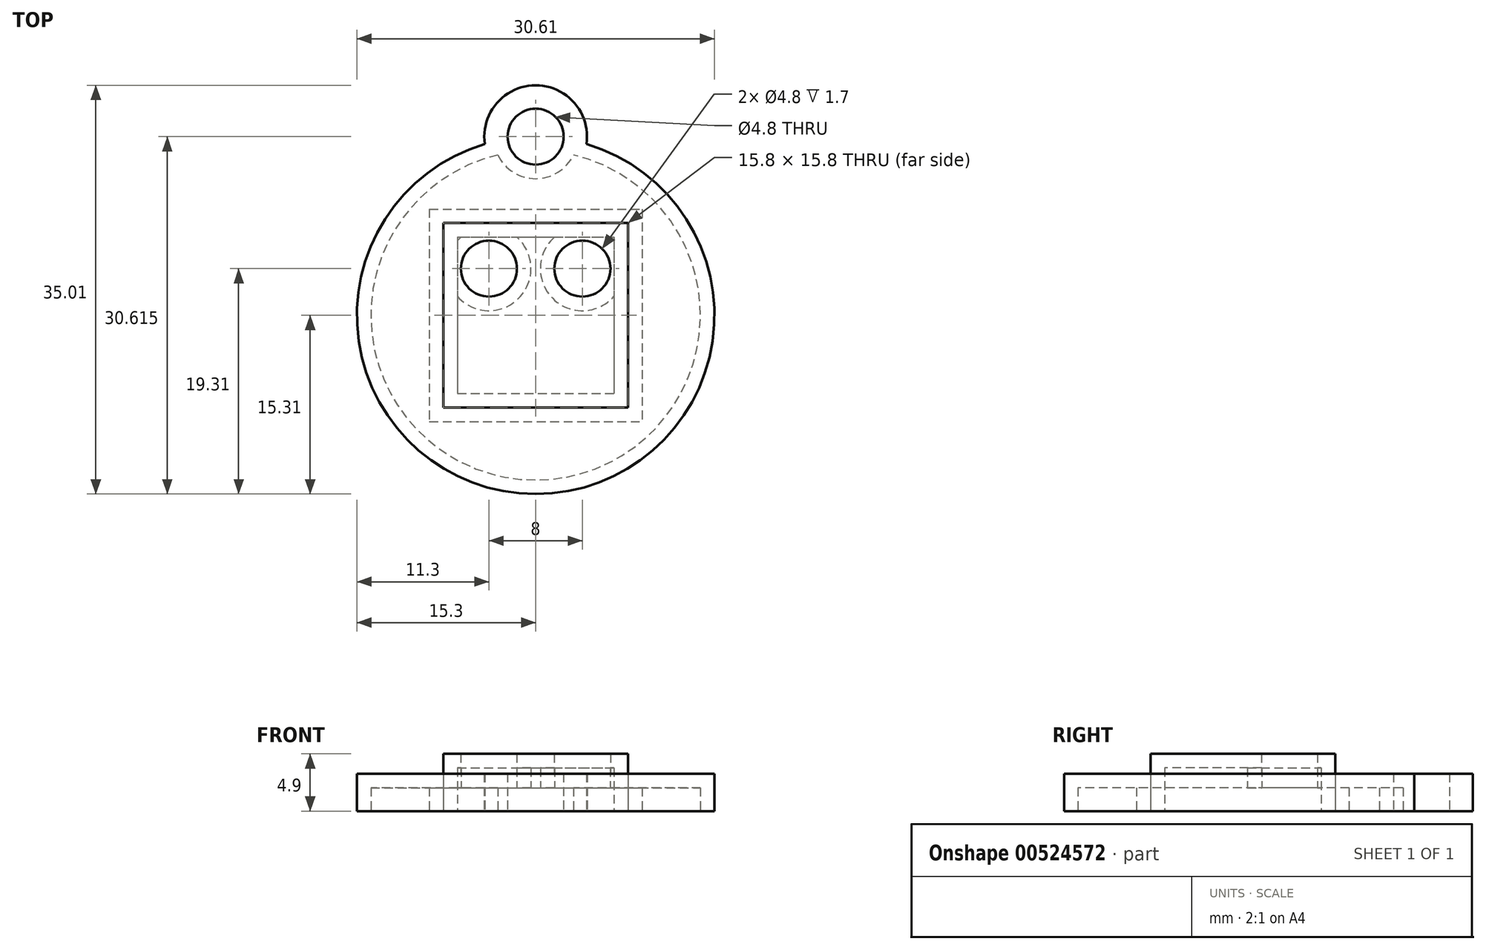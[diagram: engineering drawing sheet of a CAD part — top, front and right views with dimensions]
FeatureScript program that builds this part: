
annotation { "Feature Type Name" : "Feature", "Feature Type Description" : "" }
export const myFeature = defineFeature(function(context is Context, id is Id, definition is map)
    precondition{}
    {
        {
            var Q0;
            Q0=qCreatedBy(makeId("Top.planeOp"),FACE);
            var sketch = newSketch(context, id + "F0", { "sketchPlane" : qUnion([Q0])});
            skLineSegment(sketch, "E0.bottom", {"start": v(-7.9, 7.9) * mm, "end": v(7.9, 7.9) * mm});
            skLineSegment(sketch, "E0.top", {"start": v(-7.9, -7.9) * mm, "end": v(7.9, -7.9) * mm});
            skLineSegment(sketch, "E0.left", {"start": v(-7.9, 7.9) * mm, "end": v(-7.9, -7.9) * mm});
            skLineSegment(sketch, "E0.right", {"start": v(7.9, 7.9) * mm, "end": v(7.9, -7.9) * mm});
            skPoint(sketch, "E0.middle", {"position": v(0, 0) * mm});
            skSolve(sketch);
        }
        {
            var Q0;
            Q0=makeQuery(id+"F0.imprint","IMPRINT",FACE,{"disambiguationData":[TD([[makeQuery(id+"F0.imprint","IMPRINT",EDGE,{"derivedFrom":sQuery(id+"F0.wireOp",EDGE,"E0.bottom")}),-1.0]])]});
            extrude(context, id + "F1", {"entities" : qUnion([Q0]), "depth" : 3.2 * mm, "offsetDistance" : 25 * mm});
        }
        {
            var Q0;
            Q0=makeQuery(id+"F1.opExtrude","CAP_FACE",FACE,{"disambiguationData":[OSD([sQuery(id+"F0.wireOp",EDGE,"E0.bottom"),sQuery(id+"F0.wireOp",EDGE,"E0.top"),sQuery(id+"F0.wireOp",EDGE,"E0.left"),sQuery(id+"F0.wireOp",EDGE,"E0.right")])],"isStart":false});
            var sketch = newSketch(context, id + "F2", { "sketchPlane" : qUnion([Q0])});
            skCircle(sketch, "E1", {"center": v(-4, -4) * mm, "radius": 2.4 * mm});
            skCircle(sketch, "E2", {"center": v(4, -4) * mm, "radius": 2.4 * mm});
            skLineSegment(sketch, "E3", {"start": v(1.5, 0) * mm, "end": v(-1.5, 0) * mm, "construction": true});
            skLineSegment(sketch, "E4", {"start": v(0, -1.55) * mm, "end": v(0, 1.55) * mm, "construction": true});
            skLineSegment(sketch, "E5", {"start": v(-4, -4) * mm, "end": v(4, -4) * mm, "construction": true});
            skPoint(sketch, "E6", {"position": v(0, -4) * mm});
            skCircle(sketch, "E7.MirrorC", {"center": v(-4, 4) * mm, "radius": 2.4 * mm});
            skCircle(sketch, "E8.MirrorC", {"center": v(4, 4) * mm, "radius": 2.4 * mm});
            skLineSegment(sketch, "E9.MirrorCS", {"start": v(-4, 4) * mm, "end": v(4, 4) * mm, "construction": true});
            skPoint(sketch, "E10.MirrorP", {"position": v(0, 4) * mm});
            skPoint(sketch, "E11", {"position": v(-10.7, -6.83) * mm});
            skSolve(sketch);
        }
        {
            var Q0;
            Q0=makeQuery(id+"F2.imprint","IMPRINT",FACE,{"disambiguationData":[TD([[makeQuery(id+"F2.imprint","IMPRINT",EDGE,{"derivedFrom":sQuery(id+"F2.wireOp",EDGE,"E1")}),1.0]])]});
            var Q1;
            Q1=makeQuery(id+"F2.imprint","IMPRINT",FACE,{"disambiguationData":[TD([[makeQuery(id+"F2.imprint","IMPRINT",EDGE,{"derivedFrom":sQuery(id+"F2.wireOp",EDGE,"E7.MirrorC")}),-1.0]])]});
            var Q2;
            Q2=makeQuery(id+"F2.imprint","IMPRINT",FACE,{"disambiguationData":[TD([[makeQuery(id+"F2.imprint","IMPRINT",EDGE,{"derivedFrom":sQuery(id+"F2.wireOp",EDGE,"E8.MirrorC")}),-1.0]])]});
            var Q3;
            Q3=makeQuery(id+"F2.imprint","IMPRINT",FACE,{"disambiguationData":[TD([[makeQuery(id+"F2.imprint","IMPRINT",EDGE,{"derivedFrom":sQuery(id+"F2.wireOp",EDGE,"E2")}),1.0]])]});
            extrude(context, id + "F3", {"entities" : qUnion([Q0, Q1, Q2, Q3]), "operationType" : NewBodyOperationType.ADD, "depth" : 1.7 * mm, "offsetDistance" : 25 * mm});
        }
        {
            var Q0;
            Q0=qCreatedBy(makeId("Top.planeOp"),FACE);
            var sketch = newSketch(context, id + "F4", { "sketchPlane" : qUnion([Q0])});
            skArc(sketch, "E12", {"start": v(-4.35, 14.67) * mm, "mid": v(0, -15.3) * mm, "end": v(4.35, 14.67) * mm});
            skCircle(sketch, "E13", {"center": v(0, 15.3) * mm, "radius": 2.4 * mm});
            skArc(sketch, "E14.0", {"start": v(4.35, 14.67) * mm, "mid": v(0, 19.7) * mm, "end": v(-4.35, 14.67) * mm});
            skLineSegment(sketch, "E15.0", {"start": v(-7.9, 7.9) * mm, "end": v(7.9, 7.9) * mm});
            skLineSegment(sketch, "E16.0", {"start": v(-7.9, 7.9) * mm, "end": v(-7.9, -7.9) * mm});
            skLineSegment(sketch, "E17.0", {"start": v(-7.9, -7.9) * mm, "end": v(7.9, -7.9) * mm});
            skLineSegment(sketch, "E18.0", {"start": v(7.9, 7.9) * mm, "end": v(7.9, -7.9) * mm});
            skSolve(sketch);
        }
        {
            var Q0;
            Q0=makeQuery(id+"F4.imprint","IMPRINT",FACE,{"disambiguationData":[TD([[makeQuery(id+"F4.imprint","IMPRINT",EDGE,{"derivedFrom":sQuery(id+"F4.wireOp",EDGE,"E12")}),1.0]])]});
            extrude(context, id + "F5", {"entities" : qUnion([Q0]), "depth" : 3.2 * mm, "offsetDistance" : 25 * mm});
        }
        {
            var Q0;
            Q0=makeQuery(id+"F5.opExtrude","CAP_FACE",FACE,{"disambiguationData":[OSD([sQuery(id+"F4.wireOp",EDGE,"E12"),sQuery(id+"F4.wireOp",EDGE,"E13"),sQuery(id+"F4.wireOp",EDGE,"E14.0"),sQuery(id+"F4.wireOp",EDGE,"E15.0"),sQuery(id+"F4.wireOp",EDGE,"E16.0"),sQuery(id+"F4.wireOp",EDGE,"E17.0"),sQuery(id+"F4.wireOp",EDGE,"E18.0")])],"isStart":true});
            shell(context, id + "F6", {"entities" : qUnion([Q0]), "thickness" : 1.2 * mm});
        }
        {
            var Q0;
            Q0=makeQuery(id+"F1.opExtrude","CAP_FACE",FACE,{"disambiguationData":[OSD([sQuery(id+"F0.wireOp",EDGE,"E0.bottom"),sQuery(id+"F0.wireOp",EDGE,"E0.top"),sQuery(id+"F0.wireOp",EDGE,"E0.left"),sQuery(id+"F0.wireOp",EDGE,"E0.right")])],"isStart":true});
            shell(context, id + "F7", {"entities" : qUnion([Q0]), "thickness" : 1.2 * mm});
        }
    });
